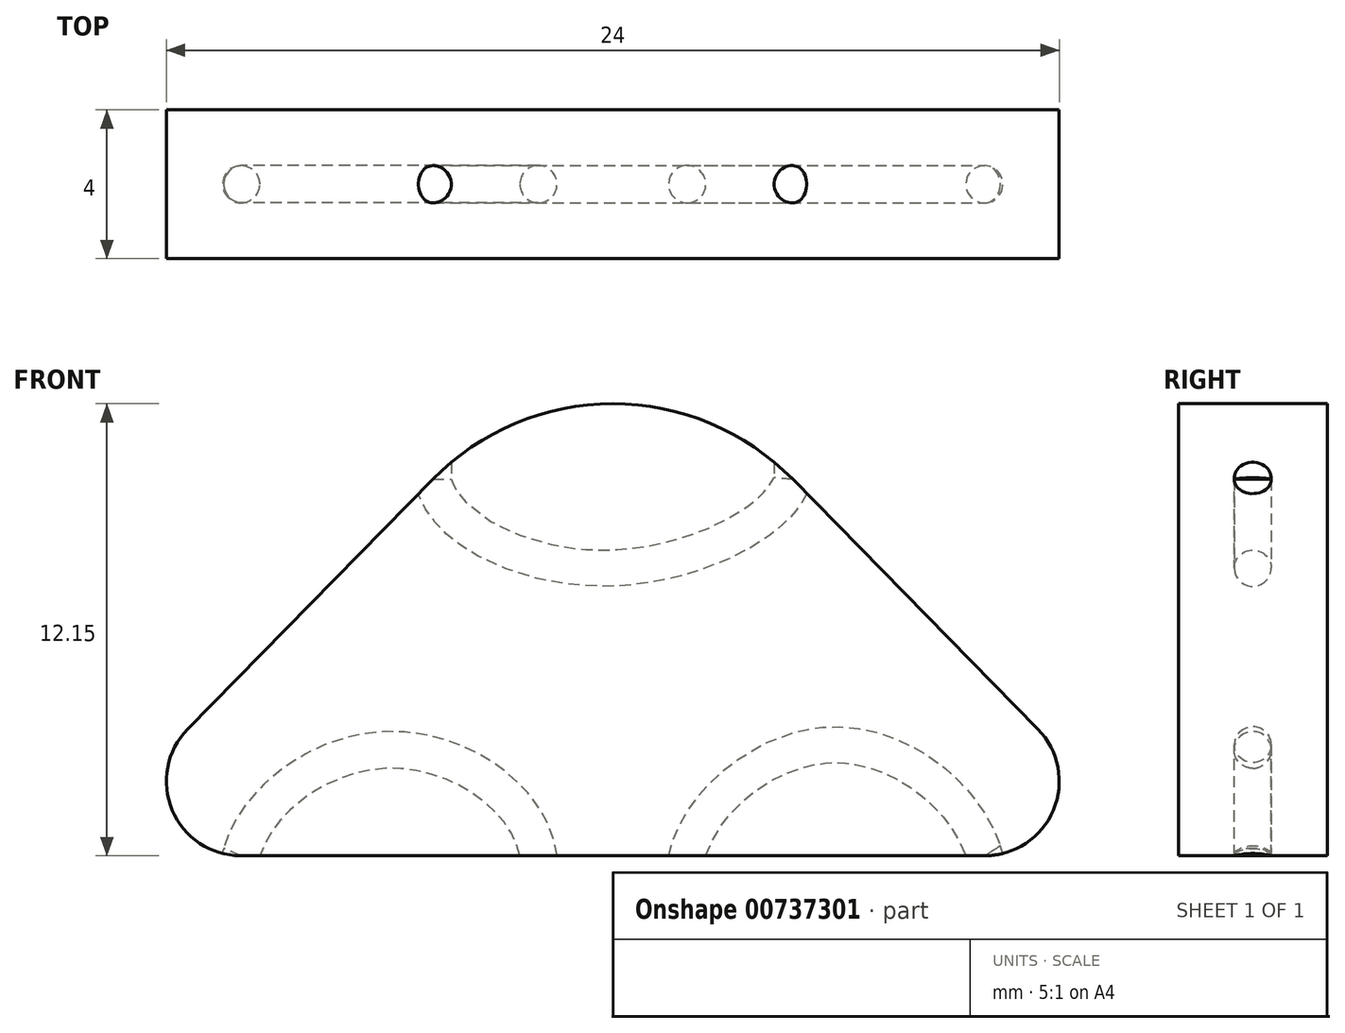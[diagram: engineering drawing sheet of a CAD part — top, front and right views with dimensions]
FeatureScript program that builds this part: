
annotation { "Feature Type Name" : "Feature", "Feature Type Description" : "" }
export const myFeature = defineFeature(function(context is Context, id is Id, definition is map)
    precondition{}
    {
        {
            var Q0;
            Q0=qCreatedBy(makeId("Front.planeOp"),FACE);
            var sketch = newSketch(context, id + "F0", { "sketchPlane" : qUnion([Q0])});
            skLineSegment(sketch, "E0", {"start": v(-41.18, -9.64) * mm, "end": v(-21.18, -9.64) * mm});
            skArc(sketch, "E1", {"start": v(-42.6, -6.24) * mm, "mid": v(-43.03, -8.42) * mm, "end": v(-41.18, -9.64) * mm});
            skArc(sketch, "E2", {"start": v(-21.18, -9.64) * mm, "mid": v(-19.34, -8.42) * mm, "end": v(-19.75, -6.24) * mm});
            skLineSegment(sketch, "E3", {"start": v(-42.6, -6.24) * mm, "end": v(-36.02, 0.48) * mm});
            skLineSegment(sketch, "E4", {"start": v(-19.75, -6.24) * mm, "end": v(-26.34, 0.48) * mm});
            skArc(sketch, "E5", {"start": v(-26.34, 0.48) * mm, "mid": v(-31.18, 2.5) * mm, "end": v(-36.02, 0.48) * mm});
            skSolve(sketch);
        }
        {
            var Q0;
            Q0 = qSketchRegion(id + "F0", true);
            extrude(context, id + "F1", {"entities" : qUnion([Q0]), "depth" : 4 * mm, "offsetDistance" : 25 * mm});
        }
        {
            var Q0;
            Q0=makeQuery(id+"F1.opExtrude","SWEPT_FACE",FACE,{"disambiguationData":[OSD([sQuery(id+"F0.wireOp",EDGE,"E0")])]});
            var sketch = newSketch(context, id + "F2", { "sketchPlane" : qUnion([Q0])});
            skCircle(sketch, "E6", {"center": v(-33.18, 2) * mm, "radius": 0.5 * mm});
            skCircle(sketch, "E7", {"center": v(-29.18, 2) * mm, "radius": 0.5 * mm});
            skCircle(sketch, "E8", {"center": v(-21.18, 2) * mm, "radius": 0.5 * mm});
            skCircle(sketch, "E9", {"center": v(-41.18, 2) * mm, "radius": 0.5 * mm});
            skSolve(sketch);
        }
        {
            var Q0;
            Q0=makeQuery(id+"F1.opExtrude","SWEPT_EDGE",EDGE,{"disambiguationData":[OSD([sQuery(id+"F0.wireOp",EDGE,"E3"),sQuery(id+"F0.wireOp",EDGE,"E5")])]});
            cPoint(context, id + "F3", {"entities" : qUnion([Q0]), "parameter" : 0.5});
        }
        {
            var Q0;
            Q0=makeQuery(id+"F1.opExtrude","CAP_VERTEX",VERTEX,{"disambiguationData":[OSD([sQuery(id+"F0.wireOp",EDGE,"E4"),sQuery(id+"F0.wireOp",EDGE,"E5")])],"isStart":true});
            var Q1;
            Q1=makeQuery(id+"F1.opExtrude","CAP_VERTEX",VERTEX,{"disambiguationData":[OSD([sQuery(id+"F0.wireOp",EDGE,"E4"),sQuery(id+"F0.wireOp",EDGE,"E5")])],"isStart":false});
            var Q2;
            Q2 = qCreatedBy(id + "F3" ,VERTEX);
            cPlane(context, id + "F4", {"entities" : qUnion([Q0, Q1, Q2]), "cplaneType" : CPlaneType.THREE_POINT, "offset" : 25 * mm, "width" : 150 * mm, "height" : 150 * mm});
        }
        {
            var Q0;
            Q0=qCreatedBy(id+"F4.planeOp",FACE);
            var sketch = newSketch(context, id + "F5", { "sketchPlane" : qUnion([Q0])});
            skCircle(sketch, "E10", {"center": v(-26.34, -2) * mm, "radius": 0.5 * mm});
            skCircle(sketch, "E11", {"center": v(-36.02, -2) * mm, "radius": 0.5 * mm});
            skSolve(sketch);
        }
        {
            var Q0;
            Q0=makeQuery(id+"F1.opExtrude","SWEPT_EDGE",EDGE,{"disambiguationData":[OSD([sQuery(id+"F0.wireOp",EDGE,"E3"),sQuery(id+"F0.wireOp",EDGE,"E5")])]});
            cPoint(context, id + "F6", {"entities" : qUnion([Q0]), "parameter" : 0.5});
        }
        {
            var Q0;
            Q0=sQuery(id+"F2.wireOp",VERTEX,"E6.center");
            var Q1;
            Q1=sQuery(id+"F2.wireOp",VERTEX,"E7.center");
            var Q2;
            Q2 = qCreatedBy(id + "F6" ,VERTEX);
            cPlane(context, id + "F7", {"entities" : qUnion([Q0, Q1, Q2]), "cplaneType" : CPlaneType.THREE_POINT, "offset" : 25 * mm, "width" : 150 * mm, "height" : 150 * mm});
        }
        {
            var Q0;
            Q0=qCreatedBy(id+"F7.planeOp",FACE);
            var sketch = newSketch(context, id + "F8", { "sketchPlane" : qUnion([Q0])});
            skFitSpline(sketch, "E12", {"points": [v(41.18, -9.64) * mm, v(37.1, -6.8) * mm, v(33.18, -9.64) * mm], "startDerivative": vector(-2.44, 9.27) * mm, "endDerivative": vector(-1.41, -9.35) * mm});
            skFitSpline(sketch, "E13", {"points": [v(29.18, -9.64) * mm, v(25.31, -6.66) * mm, v(21.18, -9.64) * mm], "startDerivative": vector(-2.44, 9.27) * mm, "endDerivative": vector(-3.26, -10.1) * mm});
            skFitSpline(sketch, "E14", {"points": [v(26.34, 0.48) * mm, v(31.32, -1.9) * mm, v(36.02, 0.48) * mm], "startDerivative": vector(2.14, -7.04) * mm, "endDerivative": vector(1.94, 8.48) * mm});
            skSolve(sketch);
        }
        {
            var Q0;
            Q0 = qSketchRegion(id + "F5", true);
            var Q1;
            Q1=sQuery(id+"F8.wireOp",EDGE,"E14");
            sweep(context, id + "F9", {"operationType" : NewBodyOperationType.REMOVE, "profiles" : qUnion([Q0]), "path" : qUnion([Q1])});
        }
        {
            var Q0;
            Q0 = qSketchRegion(id + "F5", true);
            extrude(context, id + "F10", {"entities" : qUnion([Q0]), "operationType" : NewBodyOperationType.REMOVE, "depth" : 25 * mm, "offsetDistance" : 25 * mm});
        }
        {
            var Q0;
            {var subQ0=sQuery(id+"F2.wireOp",EDGE,"E9");var subQ1=makeQuery(id+"F1.opExtrude","SWEPT_EDGE",EDGE,{"disambiguationData":[OSD([sQuery(id+"F0.wireOp",EDGE,"E0"),sQuery(id+"F0.wireOp",EDGE,"E1")])]});var subQ2=makeQuery(id+"F2.imprint","INTERSECT",VERTEX,{"disambiguationData":[OD(0.0)],"derivedFrom":[subQ1,subQ0]});Q0=makeQuery(id+"F2.imprint","IMPRINT",FACE,{"disambiguationData":[TD([[makeQuery(id+"F2.imprint","IMPRINT",EDGE,{"disambiguationData":[TD([[subQ2,1.0]])],"derivedFrom":subQ0}),1.0]])]});}
            var Q1;
            {var subQ0=sQuery(id+"F2.wireOp",EDGE,"E9");var subQ1=makeQuery(id+"F1.opExtrude","SWEPT_EDGE",EDGE,{"disambiguationData":[OSD([sQuery(id+"F0.wireOp",EDGE,"E0"),sQuery(id+"F0.wireOp",EDGE,"E1")])]});var subQ2=makeQuery(id+"F2.imprint","INTERSECT",VERTEX,{"disambiguationData":[OD(0.0)],"derivedFrom":[subQ1,subQ0]});Q1=makeQuery(id+"F2.imprint","IMPRINT",FACE,{"disambiguationData":[TD([[makeQuery(id+"F2.imprint","IMPRINT",EDGE,{"disambiguationData":[TD([[subQ2,-1.0]])],"derivedFrom":subQ0}),1.0]])]});}
            var Q2;
            Q2=makeQuery(id+"F2.imprint","IMPRINT",FACE,{"disambiguationData":[TD([[makeQuery(id+"F2.imprint","IMPRINT",EDGE,{"derivedFrom":sQuery(id+"F2.wireOp",EDGE,"E6")}),1.0]])]});
            var Q3;
            Q3=sQuery(id+"F8.wireOp",EDGE,"E12");
            sweep(context, id + "F11", {"operationType" : NewBodyOperationType.REMOVE, "profiles" : qUnion([Q0, Q1, Q2]), "path" : qUnion([Q3])});
        }
        {
            var Q0;
            {var subQ0=sQuery(id+"F2.wireOp",EDGE,"E8");var subQ1=makeQuery(id+"F1.opExtrude","SWEPT_EDGE",EDGE,{"disambiguationData":[OSD([sQuery(id+"F0.wireOp",EDGE,"E0"),sQuery(id+"F0.wireOp",EDGE,"E2")])]});var subQ2=makeQuery(id+"F2.imprint","INTERSECT",VERTEX,{"disambiguationData":[OD(0.0)],"derivedFrom":[subQ1,subQ0]});Q0=makeQuery(id+"F2.imprint","IMPRINT",FACE,{"disambiguationData":[TD([[makeQuery(id+"F2.imprint","IMPRINT",EDGE,{"disambiguationData":[TD([[subQ2,-1.0]])],"derivedFrom":subQ0}),1.0]])]});}
            var Q1;
            {var subQ0=sQuery(id+"F2.wireOp",EDGE,"E8");var subQ1=makeQuery(id+"F1.opExtrude","SWEPT_EDGE",EDGE,{"disambiguationData":[OSD([sQuery(id+"F0.wireOp",EDGE,"E0"),sQuery(id+"F0.wireOp",EDGE,"E2")])]});var subQ2=makeQuery(id+"F2.imprint","INTERSECT",VERTEX,{"disambiguationData":[OD(0.0)],"derivedFrom":[subQ1,subQ0]});Q1=makeQuery(id+"F2.imprint","IMPRINT",FACE,{"disambiguationData":[TD([[makeQuery(id+"F2.imprint","IMPRINT",EDGE,{"disambiguationData":[TD([[subQ2,1.0]])],"derivedFrom":subQ0}),1.0]])]});}
            var Q2;
            Q2=makeQuery(id+"F2.imprint","IMPRINT",FACE,{"disambiguationData":[TD([[makeQuery(id+"F2.imprint","IMPRINT",EDGE,{"derivedFrom":sQuery(id+"F2.wireOp",EDGE,"E7")}),1.0]])]});
            var Q3;
            Q3=sQuery(id+"F8.wireOp",EDGE,"E13");
            sweep(context, id + "F12", {"operationType" : NewBodyOperationType.REMOVE, "profiles" : qUnion([Q0, Q1, Q2]), "path" : qUnion([Q3])});
        }
    });
